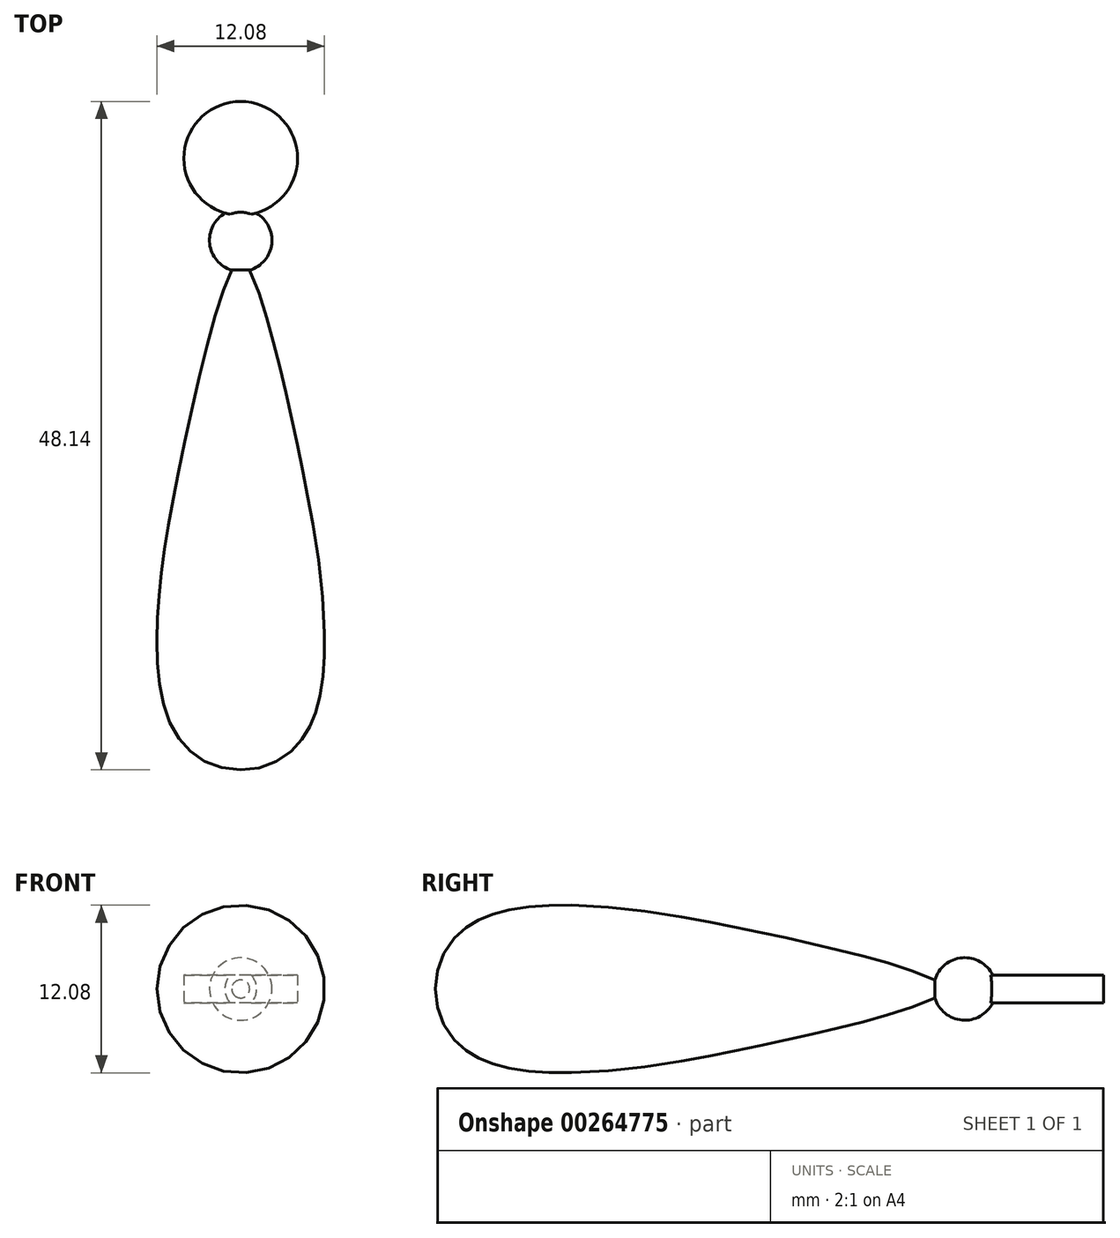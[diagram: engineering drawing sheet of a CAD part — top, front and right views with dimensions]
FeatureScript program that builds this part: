
annotation { "Feature Type Name" : "Feature", "Feature Type Description" : "" }
export const myFeature = defineFeature(function(context is Context, id is Id, definition is map)
    precondition{}
    {
        {
            var Q0;
            Q0=qCreatedBy(makeId("Top.planeOp"),FACE);
            var sketch = newSketch(context, id + "F0", { "sketchPlane" : qUnion([Q0])});
            skFitSpline(sketch, "E0", {"points": [v(0, 24.53) * mm, v(-4.1, 10.83) * mm, v(-5.98, -1.4) * mm, v(-4.86, -9.57) * mm, v(0, -12.47) * mm], "startDerivative": vector(-13.57, -13.48) * mm, "endDerivative": vector(35.47, -0.14) * mm});
            skFitSpline(sketch, "E1.MirrorCS", {"points": [v(0, 24.53) * mm, v(4.1, 10.83) * mm, v(5.98, -1.4) * mm, v(4.86, -9.57) * mm, v(0, -12.47) * mm], "startDerivative": vector(13.57, -13.48) * mm, "endDerivative": vector(-35.47, -0.14) * mm});
            skLineSegment(sketch, "E2", {"start": v(0, 24.53) * mm, "end": v(0, -12.47) * mm});
            skSolve(sketch);
        }
        {
            var Q0;
            Q0=makeQuery(id+"F0.imprint","IMPRINT",FACE,{"disambiguationData":[TD([[makeQuery(id+"F0.imprint","IMPRINT",EDGE,{"derivedFrom":sQuery(id+"F0.wireOp",EDGE,"E0")}),1.0]])]});
            var Q1;
            Q1=sQuery(id+"F0.wireOp",EDGE,"E2");
            revolve(context, id + "F1", {"surfaceOperationType" : NewSurfaceOperationType.NEW, "entities" : qUnion([Q0]), "axis" : qUnion([Q1]), "revolveType" : RevolveType.FULL});
        }
        {
            var Q0;
            Q0=qCreatedBy(makeId("Top.planeOp"),FACE);
            var sketch = newSketch(context, id + "F2", { "sketchPlane" : qUnion([Q0])});
            skCircle(sketch, "E3", {"center": v(0, 25.68) * mm, "radius": 2.25 * mm});
            skCircle(sketch, "E4", {"center": v(0, 31.58) * mm, "radius": 4.1 * mm});
            skLineSegment(sketch, "E5", {"start": v(0, 23.43) * mm, "end": v(0, 27.93) * mm});
            skSolve(sketch);
        }
        {
            var Q0;
            {var subQ0=sQuery(id+"F2.wireOp",EDGE,"E5");var subQ1=sQuery(id+"F2.wireOp",EDGE,"E3");var subQ2=makeQuery(id+"F2.imprint","INTERSECT",VERTEX,{"disambiguationData":[OD(0.0)],"derivedFrom":[subQ1,subQ0]});Q0=makeQuery(id+"F2.imprint","IMPRINT",FACE,{"disambiguationData":[TD([[makeQuery(id+"F2.imprint","IMPRINT",EDGE,{"disambiguationData":[TD([[subQ2,1.0]])],"derivedFrom":subQ1}),1.0]])]});}
            var Q1;
            {var subQ0=sQuery(id+"F2.wireOp",EDGE,"E5");var subQ1=sQuery(id+"F2.wireOp",EDGE,"E3");var subQ2=makeQuery(id+"F2.imprint","INTERSECT",VERTEX,{"disambiguationData":[OD(1.0)],"derivedFrom":[subQ1,subQ0]});Q1=makeQuery(id+"F2.imprint","IMPRINT",FACE,{"disambiguationData":[TD([[makeQuery(id+"F2.imprint","IMPRINT",EDGE,{"disambiguationData":[TD([[subQ2,-1.0]])],"derivedFrom":subQ1}),1.0]])]});}
            var Q2;
            Q2=sQuery(id+"F2.wireOp",EDGE,"E5");
            revolve(context, id + "F3", {"operationType" : NewBodyOperationType.ADD, "surfaceOperationType" : NewSurfaceOperationType.NEW, "entities" : qUnion([Q0, Q1]), "axis" : qUnion([Q2]), "revolveType" : RevolveType.FULL});
        }
        {
            var Q0;
            {var subQ0=sQuery(id+"F2.wireOp",EDGE,"E3");var subQ1=makeQuery(id+"F2.imprint","INTERSECT",VERTEX,{"disambiguationData":[OD(1.0)],"derivedFrom":[subQ0,sQuery(id+"F2.wireOp",EDGE,"E5")]});Q0=makeQuery(id+"F2.imprint","IMPRINT",FACE,{"disambiguationData":[TD([[makeQuery(id+"F2.imprint","IMPRINT",EDGE,{"disambiguationData":[TD([[subQ1,1.0]])],"derivedFrom":subQ0}),-1.0]])]});}
            var Q1;
            {var subQ0=sQuery(id+"F2.wireOp",EDGE,"E5");var subQ1=sQuery(id+"F2.wireOp",EDGE,"E3");var subQ2=makeQuery(id+"F2.imprint","INTERSECT",VERTEX,{"disambiguationData":[OD(1.0)],"derivedFrom":[subQ1,subQ0]});Q1=makeQuery(id+"F2.imprint","IMPRINT",FACE,{"disambiguationData":[TD([[makeQuery(id+"F2.imprint","IMPRINT",EDGE,{"disambiguationData":[TD([[subQ2,1.0]])],"derivedFrom":subQ1}),1.0]])]});}
            var Q2;
            {var subQ0=sQuery(id+"F2.wireOp",EDGE,"E5");var subQ1=sQuery(id+"F2.wireOp",EDGE,"E3");var subQ2=makeQuery(id+"F2.imprint","INTERSECT",VERTEX,{"disambiguationData":[OD(1.0)],"derivedFrom":[subQ1,subQ0]});Q2=makeQuery(id+"F2.imprint","IMPRINT",FACE,{"disambiguationData":[TD([[makeQuery(id+"F2.imprint","IMPRINT",EDGE,{"disambiguationData":[TD([[subQ2,-1.0]])],"derivedFrom":subQ1}),1.0]])]});}
            extrude(context, id + "F4", {"entities" : qUnion([Q0, Q1, Q2]), "operationType" : NewBodyOperationType.ADD, "depth" : 1 * mm, "offsetDistance" : 25 * mm, "hasSecondDirection" : true, "secondDirectionOppositeDirection" : true, "secondDirectionDepth" : 1 * mm});
        }
    });
